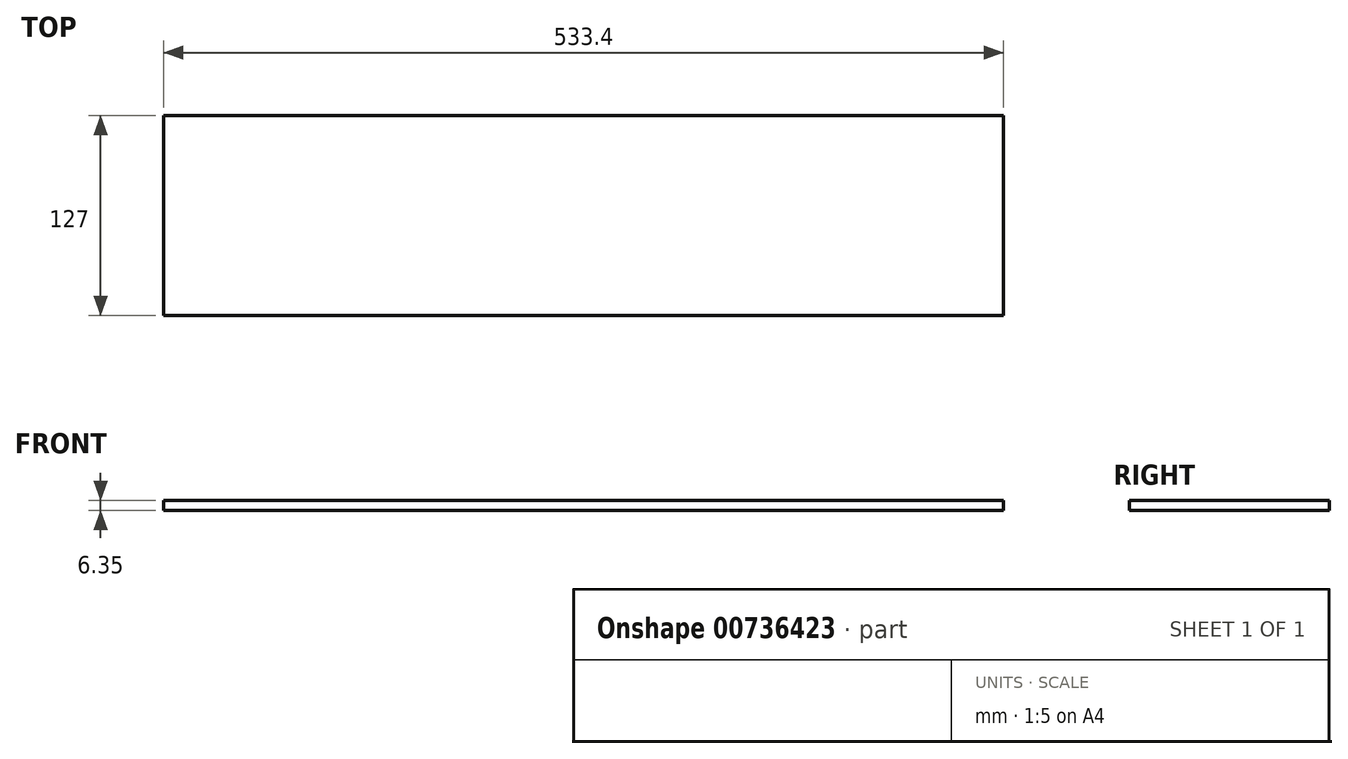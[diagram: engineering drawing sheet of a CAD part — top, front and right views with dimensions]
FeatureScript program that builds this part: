
annotation { "Feature Type Name" : "Feature", "Feature Type Description" : "" }
export const myFeature = defineFeature(function(context is Context, id is Id, definition is map)
    precondition{}
    {
        {
            var Q0;
            Q0=qCreatedBy(makeId("Top.planeOp"),FACE);
            var sketch = newSketch(context, id + "F0", { "sketchPlane" : qUnion([Q0])});
            skLineSegment(sketch, "E0.bottom", {"start": v(-266.7, 63.5) * mm, "end": v(266.7, 63.5) * mm});
            skLineSegment(sketch, "E0.top", {"start": v(-266.7, -63.5) * mm, "end": v(266.7, -63.5) * mm});
            skLineSegment(sketch, "E0.left", {"start": v(-266.7, 63.5) * mm, "end": v(-266.7, -63.5) * mm});
            skLineSegment(sketch, "E0.right", {"start": v(266.7, 63.5) * mm, "end": v(266.7, -63.5) * mm});
            skSolve(sketch);
        }
        {
            var Q0;
            Q0=makeQuery(id+"F0.imprint","IMPRINT",FACE,{"disambiguationData":[TD([[makeQuery(id+"F0.imprint","IMPRINT",EDGE,{"derivedFrom":sQuery(id+"F0.wireOp",EDGE,"E0.bottom")}),-1.0]])]});
            extrude(context, id + "F1", {"entities" : qUnion([Q0]), "depth" : 6.35 * mm, "offsetDistance" : 25.4 * mm});
        }
    });
